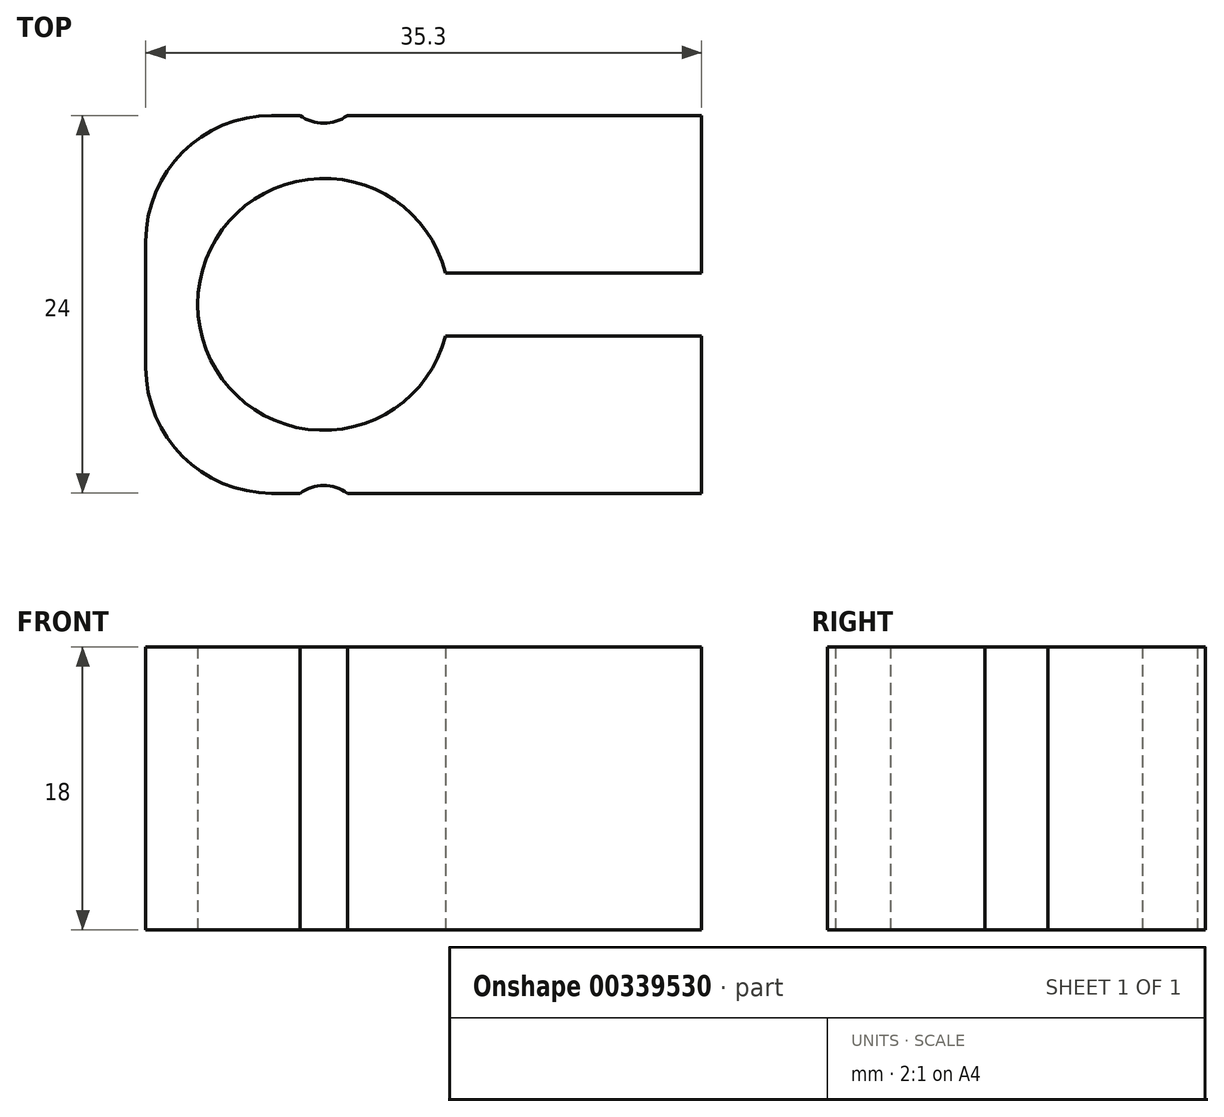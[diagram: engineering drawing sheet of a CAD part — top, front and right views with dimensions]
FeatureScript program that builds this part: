
annotation { "Feature Type Name" : "Feature", "Feature Type Description" : "" }
export const myFeature = defineFeature(function(context is Context, id is Id, definition is map)
    precondition{}
    {
        {
            var Q0;
            Q0=qCreatedBy(makeId("Top.planeOp"),FACE);
            var sketch = newSketch(context, id + "F0", { "sketchPlane" : qUnion([Q0])});
            skCircle(sketch, "E0", {"center": v(22.17, 14.46) * mm, "radius": 8 * mm});
            skLineSegment(sketch, "E1.right", {"start": v(46.17, 32.46) * mm, "end": v(46.17, -3.54) * mm});
            skLineSegment(sketch, "E2", {"start": v(22.17, -3.54) * mm, "end": v(22.17, 32.46) * mm, "construction": true});
            skCircle(sketch, "E3", {"center": v(22.17, 0.46) * mm, "radius": 2.5 * mm});
            skCircle(sketch, "E4", {"center": v(22.17, 28.46) * mm, "radius": 2.5 * mm});
            skLineSegment(sketch, "E5", {"start": v(10.87, -3.54) * mm, "end": v(10.87, 32.46) * mm});
            skLineSegment(sketch, "E6", {"start": v(10.87, 32.46) * mm, "end": v(46.17, 32.46) * mm});
            skLineSegment(sketch, "E7", {"start": v(10.87, -3.54) * mm, "end": v(46.17, -3.54) * mm});
            skLineSegment(sketch, "E8.bottom", {"start": v(51.26, 12.46) * mm, "end": v(-6.92, 12.46) * mm});
            skLineSegment(sketch, "E8.top", {"start": v(51.26, 16.46) * mm, "end": v(-6.92, 16.46) * mm});
            skLineSegment(sketch, "E8.left", {"start": v(51.26, 12.46) * mm, "end": v(51.26, 16.46) * mm});
            skLineSegment(sketch, "E8.right", {"start": v(-6.92, 12.46) * mm, "end": v(-6.92, 16.46) * mm});
            skLineSegment(sketch, "E9.bottom", {"start": v(-7.83, 26.46) * mm, "end": v(52.17, 26.46) * mm});
            skLineSegment(sketch, "E9.top", {"start": v(-7.83, 2.46) * mm, "end": v(52.17, 2.46) * mm});
            skLineSegment(sketch, "E9.left", {"start": v(-7.83, 26.46) * mm, "end": v(-7.83, 2.46) * mm});
            skLineSegment(sketch, "E9.right", {"start": v(52.17, 26.46) * mm, "end": v(52.17, 2.46) * mm});
            skLineSegment(sketch, "E10", {"start": v(34.17, 32.46) * mm, "end": v(34.17, -3.54) * mm});
            skSolve(sketch);
        }
        {
            var Q0;
            {var subQ0=sQuery(id+"F0.wireOp",EDGE,"E9.top");var subQ3=sQuery(id+"F0.wireOp",EDGE,"E3");var subQ4=makeQuery(id+"F0.imprint","INTERSECT",VERTEX,{"disambiguationData":[OD(0.0)],"derivedFrom":[subQ3,subQ0]});Q0=makeQuery(id+"F0.imprint","IMPRINT",FACE,{"disambiguationData":[TD([[makeQuery(id+"F0.imprint","IMPRINT",EDGE,{"disambiguationData":[TD([[subQ4,-1.0]])],"derivedFrom":subQ3}),-1.0]])]});}
            var Q1;
            {var subQ5=sQuery(id+"F0.wireOp",EDGE,"E9.bottom");var subQ7=sQuery(id+"F0.wireOp",EDGE,"E4");var subQ8=makeQuery(id+"F0.imprint","INTERSECT",VERTEX,{"disambiguationData":[OD(0.0)],"derivedFrom":[subQ7,subQ5]});Q1=makeQuery(id+"F0.imprint","IMPRINT",FACE,{"disambiguationData":[TD([[makeQuery(id+"F0.imprint","IMPRINT",EDGE,{"disambiguationData":[TD([[subQ8,1.0]])],"derivedFrom":subQ7}),-1.0]])]});}
            var Q2;
            {var subQ0=sQuery(id+"F0.wireOp",EDGE,"E9.bottom");var subQ1=sQuery(id+"F0.wireOp",EDGE,"E1.right");var subQ2=makeQuery(id+"F0.imprint","INTERSECT",VERTEX,{"derivedFrom":[subQ1,subQ0]});Q2=makeQuery(id+"F0.imprint","IMPRINT",FACE,{"disambiguationData":[TD([[makeQuery(id+"F0.imprint","IMPRINT",EDGE,{"disambiguationData":[TD([[subQ2,-1.0]])],"derivedFrom":subQ1}),-1.0]])]});}
            var Q3;
            {var subQ0=sQuery(id+"F0.wireOp",EDGE,"E9.top");var subQ1=sQuery(id+"F0.wireOp",EDGE,"E1.right");var subQ2=makeQuery(id+"F0.imprint","INTERSECT",VERTEX,{"derivedFrom":[subQ1,subQ0]});Q3=makeQuery(id+"F0.imprint","IMPRINT",FACE,{"disambiguationData":[TD([[makeQuery(id+"F0.imprint","IMPRINT",EDGE,{"disambiguationData":[TD([[subQ2,1.0]])],"derivedFrom":subQ1}),-1.0]])]});}
            var Q4;
            {var subQ3=sQuery(id+"F0.wireOp",EDGE,"E8.top");var subQ8=sQuery(id+"F0.wireOp",EDGE,"E0");var subQ9=makeQuery(id+"F0.imprint","INTERSECT",VERTEX,{"disambiguationData":[OD(0.0)],"derivedFrom":[subQ8,subQ3]});Q4=makeQuery(id+"F0.imprint","IMPRINT",FACE,{"disambiguationData":[TD([[makeQuery(id+"F0.imprint","IMPRINT",EDGE,{"disambiguationData":[TD([[subQ9,1.0]])],"derivedFrom":subQ8}),-1.0]])]});}
            var Q5;
            {var subQ0=sQuery(id+"F0.wireOp",EDGE,"E8.bottom");var subQ1=sQuery(id+"F0.wireOp",EDGE,"E0");var subQ5=makeQuery(id+"F0.imprint","INTERSECT",VERTEX,{"disambiguationData":[OD(0.0)],"derivedFrom":[subQ1,subQ0]});Q5=makeQuery(id+"F0.imprint","IMPRINT",FACE,{"disambiguationData":[TD([[makeQuery(id+"F0.imprint","IMPRINT",EDGE,{"disambiguationData":[TD([[subQ5,-1.0]])],"derivedFrom":subQ1}),-1.0]])]});}
            var Q6;
            {var subQ0=sQuery(id+"F0.wireOp",EDGE,"E8.top");var subQ1=sQuery(id+"F0.wireOp",EDGE,"E0");var subQ2=makeQuery(id+"F0.imprint","INTERSECT",VERTEX,{"disambiguationData":[OD(0.0)],"derivedFrom":[subQ1,subQ0]});Q6=makeQuery(id+"F0.imprint","IMPRINT",FACE,{"disambiguationData":[TD([[makeQuery(id+"F0.imprint","IMPRINT",EDGE,{"disambiguationData":[TD([[subQ2,-1.0]])],"derivedFrom":subQ1}),-1.0]])]});}
            extrude(context, id + "F1", {"entities" : qUnion([Q0, Q1, Q2, Q3, Q4, Q5, Q6]), "depth" : 18 * mm, "offsetDistance" : 25 * mm});
        }
        {
            var Q0;
            Q0=makeQuery(id+"F1.opExtrude","SWEPT_EDGE",EDGE,{"disambiguationData":[OSD([sQuery(id+"F0.wireOp",EDGE,"E6"),sQuery(id+"F0.wireOp",EDGE,"E10")])]});
            var Q1;
            Q1=makeQuery(id+"F1.opExtrude","SWEPT_EDGE",EDGE,{"disambiguationData":[OSD([sQuery(id+"F0.wireOp",EDGE,"E7"),sQuery(id+"F0.wireOp",EDGE,"E10")])]});
            var Q2;
            Q2=makeQuery(id+"F1.opExtrude","SWEPT_EDGE",EDGE,{"disambiguationData":[OSD([sQuery(id+"F0.wireOp",EDGE,"E5"),sQuery(id+"F0.wireOp",EDGE,"E7")])]});
            var Q3;
            Q3=makeQuery(id+"F1.opExtrude","SWEPT_EDGE",EDGE,{"disambiguationData":[OSD([sQuery(id+"F0.wireOp",EDGE,"E5"),sQuery(id+"F0.wireOp",EDGE,"E6")])]});
            fillet(context, id + "F2", {"entities" : qUnion([Q0, Q1, Q2, Q3]), "radius" : 8 * mm, "tangentPropagation" : true, "allowEdgeOverflow" : false});
        }
    });
